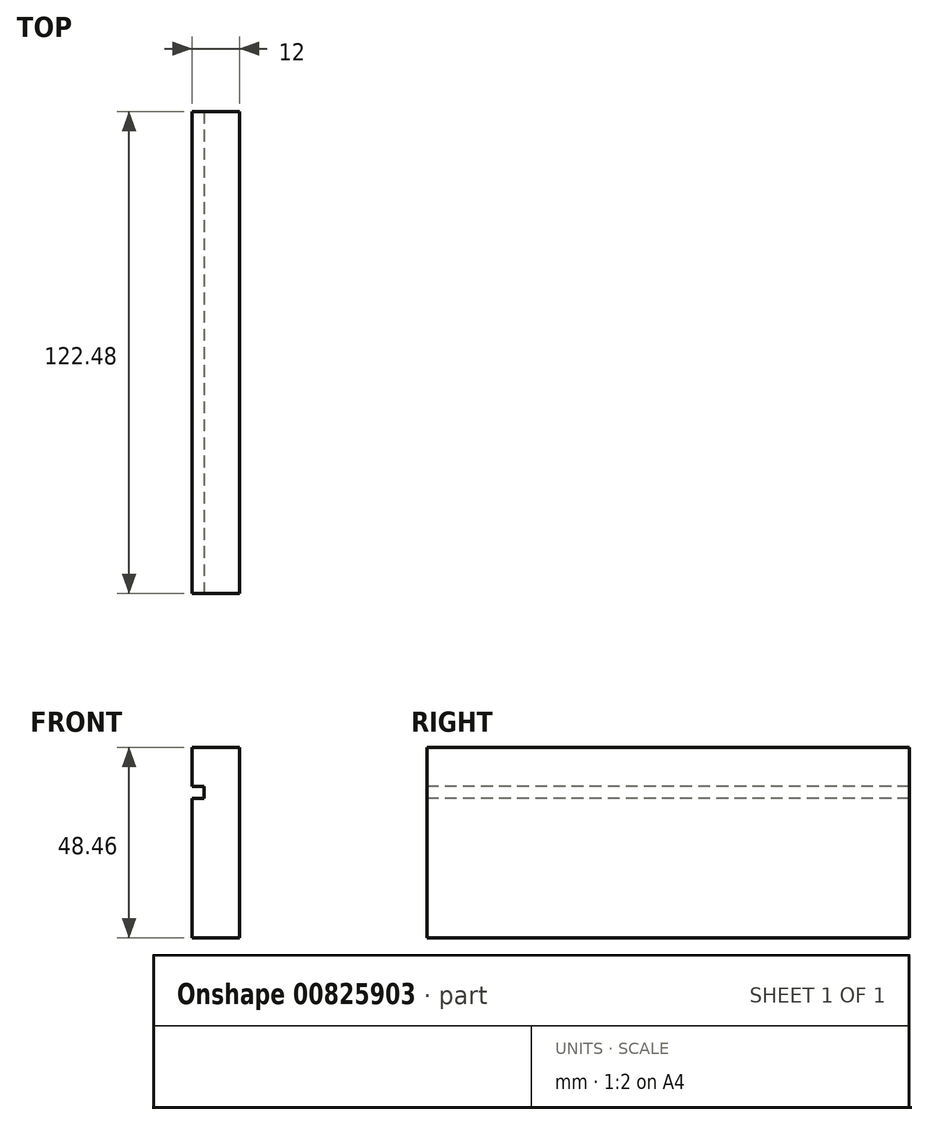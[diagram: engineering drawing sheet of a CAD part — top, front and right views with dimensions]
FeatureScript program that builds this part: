
annotation { "Feature Type Name" : "Feature", "Feature Type Description" : "" }
export const myFeature = defineFeature(function(context is Context, id is Id, definition is map)
    precondition{}
    {
        {
            var Q0;
            Q0=qCreatedBy(makeId("Right.planeOp"),FACE);
            var sketch = newSketch(context, id + "F0", { "sketchPlane" : qUnion([Q0])});
            skLineSegment(sketch, "E0.bottom", {"start": v(-61.24, 24.23) * mm, "end": v(61.24, 24.23) * mm});
            skLineSegment(sketch, "E0.top", {"start": v(-61.24, -24.23) * mm, "end": v(61.24, -24.23) * mm});
            skLineSegment(sketch, "E0.left", {"start": v(-61.24, 24.23) * mm, "end": v(-61.24, -24.23) * mm});
            skLineSegment(sketch, "E0.right", {"start": v(61.24, 24.23) * mm, "end": v(61.24, -24.23) * mm});
            skPoint(sketch, "E0.middle", {"position": v(0, 0) * mm});
            skSolve(sketch);
        }
        {
            var Q0;
            Q0=makeQuery(id+"F0.imprint","IMPRINT",FACE,{"disambiguationData":[TD([[makeQuery(id+"F0.imprint","IMPRINT",EDGE,{"derivedFrom":sQuery(id+"F0.wireOp",EDGE,"E0.bottom")}),-1.0]])]});
            extrude(context, id + "F1", {"entities" : qUnion([Q0]), "depth" : 12 * mm, "offsetDistance" : 25.4 * mm});
        }
        {
            var Q0;
            Q0=makeQuery(id+"F1.opExtrude","SWEPT_FACE",FACE,{"disambiguationData":[OSD([sQuery(id+"F0.wireOp",EDGE,"E0.left")])]});
            var sketch = newSketch(context, id + "F2", { "sketchPlane" : qUnion([Q0])});
            skLineSegment(sketch, "E1.bottom", {"start": v(0, 14.23) * mm, "end": v(3, 14.23) * mm});
            skLineSegment(sketch, "E1.top", {"start": v(0, 11.23) * mm, "end": v(3, 11.23) * mm});
            skLineSegment(sketch, "E1.left", {"start": v(0, 14.23) * mm, "end": v(0, 11.23) * mm});
            skLineSegment(sketch, "E1.right", {"start": v(3, 14.23) * mm, "end": v(3, 11.23) * mm});
            skSolve(sketch);
        }
        {
            var Q0;
            Q0 = qSketchRegion(id + "F2", true);
            extrude(context, id + "F3", {"entities" : qUnion([Q0]), "operationType" : NewBodyOperationType.REMOVE, "oppositeDirection" : true, "depth" : 30000 * mm, "offsetDistance" : 25.4 * mm});
        }
    });
